# Revit family: rba-bim-B2892
name_source: partatom
category: Specialty Equipment
revit_build: Autodesk Revit 2018 (Build: 20170223_1515(x64)
units: mm (PartAtom-declared; Revit-internal decimal feet)

## family parameters
Always vertical = No
Cut with Voids When Loaded = No
OmniClass Number = 23.40.20.21
OmniClass Title = Toilet and Bath Specialties
Part Type = Normal
Room Calculation Point = No
Round Connector Dimension = Use Diameter
Shared = Yes
Work Plane-Based = Yes

## types (1)
- B-2892
    Assembly Code = E1090900
    Capacity = Two Toilet Tissue Rolls, 10" Diameter either 3" Core or 2-1/4" Core
    Default Elevation = 1219 mm
    Description = Jumbo Twin Toilet Roll Holder
    Expected Lifespan (Years) = 0
    Installation-Fabrication = http://www.bobrick.com
    Keynote = 102813
    Maintenance Schedule (Months) = 0
    Manufacturer = Bobrick Washroom Equipment, Inc.
    Manufacturer Fax = 818-503-1930
    Manufacturer Website = http://www.bobrick.com
    Materials and Finishes = Stainless Steel Satin Finish
    Model = B2892
    Modified Issue = 20200930.01
    Product Data = http://arcat.com
    Revision = R1_10-2012
    Sales Information = http://www.bobrick.com
    Send Message = http://www.arcat.com
    URL = www.rba.com
    Unit Depth = 151 mm
    Unit Height = 289 mm
    Unit Width = 513 mm
    Warranty Duration (Years) = 0

## geometry (parser evidence)
native form markers: Blend x2, Sweep x3
no freeform markers — native parametric forms only
